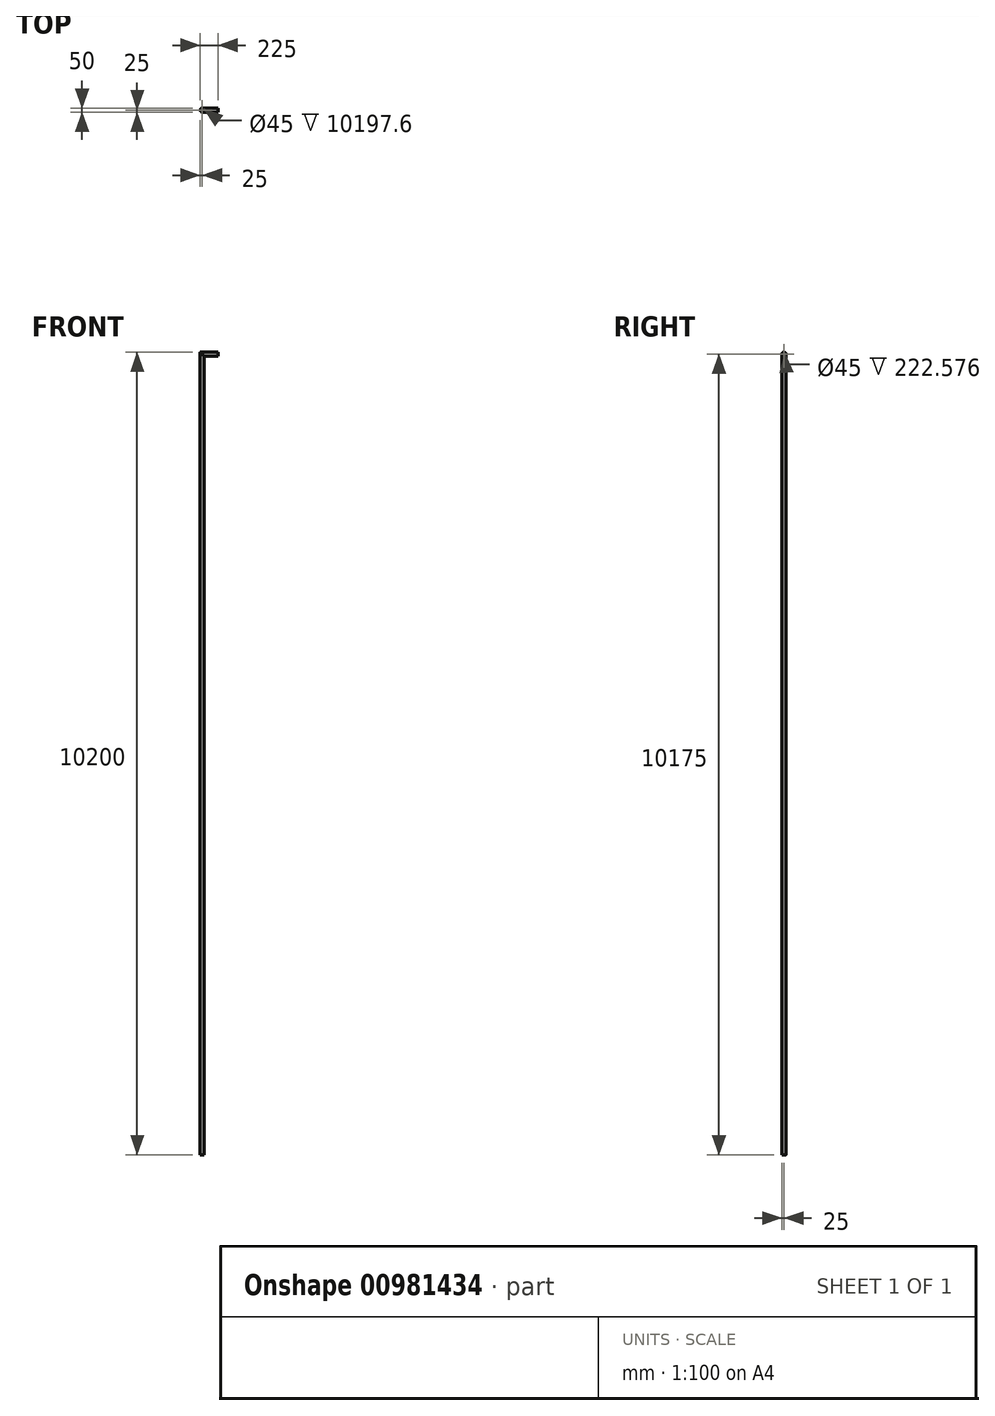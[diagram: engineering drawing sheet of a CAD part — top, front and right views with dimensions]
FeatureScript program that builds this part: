
annotation { "Feature Type Name" : "Feature", "Feature Type Description" : "" }
export const myFeature = defineFeature(function(context is Context, id is Id, definition is map)
    precondition{}
    {
        {
            var Q0;
            Q0=qCreatedBy(makeId("Front.planeOp"),FACE);
            var sketch = newSketch(context, id + "F0", { "sketchPlane" : qUnion([Q0])});
            skLineSegment(sketch, "E0.bottom", {"start": v(-25, 5100) * mm, "end": v(200, 5100) * mm});
            skLineSegment(sketch, "E0.top", {"start": v(-25, -5100) * mm, "end": v(25, -5100) * mm});
            skLineSegment(sketch, "E0.left", {"start": v(-25, 5100) * mm, "end": v(-25, -5100) * mm});
            skLineSegment(sketch, "E0.right", {"start": v(25, 5050) * mm, "end": v(25, -5100) * mm});
            skPoint(sketch, "E0.middle", {"position": v(0, 0) * mm});
            skLineSegment(sketch, "E1", {"start": v(200, 5100) * mm, "end": v(200, 5050) * mm});
            skLineSegment(sketch, "E2", {"start": v(200, 5050) * mm, "end": v(25, 5050) * mm});
            skSolve(sketch);
        }
        {
            var Q0;
            Q0 = qSketchRegion(id + "F0", true);
            extrude(context, id + "F1", {"entities" : qUnion([Q0]), "depth" : 50 * mm, "offsetDistance" : 25 * mm});
        }
        {
            var Q0;
            Q0=makeQuery(id+"F1.opExtrude","CAP_EDGE",EDGE,{"disambiguationData":[OSD([sQuery(id+"F0.wireOp",EDGE,"E0.bottom")])],"isStart":false});
            var Q1;
            Q1=makeQuery(id+"F1.opExtrude","CAP_EDGE",EDGE,{"disambiguationData":[OSD([sQuery(id+"F0.wireOp",EDGE,"E0.left")])],"isStart":false});
            var Q2;
            Q2=makeQuery(id+"F1.opExtrude","CAP_EDGE",EDGE,{"disambiguationData":[OSD([sQuery(id+"F0.wireOp",EDGE,"E2")])],"isStart":false});
            var Q3;
            Q3=makeQuery(id+"F1.opExtrude","CAP_EDGE",EDGE,{"disambiguationData":[OSD([sQuery(id+"F0.wireOp",EDGE,"E0.right")])],"isStart":false});
            var Q4;
            Q4=makeQuery(id+"F1.opExtrude","CAP_EDGE",EDGE,{"disambiguationData":[OSD([sQuery(id+"F0.wireOp",EDGE,"E2")])],"isStart":true});
            var Q5;
            Q5=makeQuery(id+"F1.opExtrude","CAP_EDGE",EDGE,{"disambiguationData":[OSD([sQuery(id+"F0.wireOp",EDGE,"E0.right")])],"isStart":true});
            var Q6;
            Q6=makeQuery(id+"F1.opExtrude","CAP_EDGE",EDGE,{"disambiguationData":[OSD([sQuery(id+"F0.wireOp",EDGE,"E0.bottom")])],"isStart":true});
            var Q7;
            Q7=makeQuery(id+"F1.opExtrude","CAP_EDGE",EDGE,{"disambiguationData":[OSD([sQuery(id+"F0.wireOp",EDGE,"E0.left")])],"isStart":true});
            fillet(context, id + "F2", {"entities" : qUnion([Q0, Q1, Q2, Q3, Q4, Q5, Q6, Q7]), "radius" : 25 * mm, "tangentPropagation" : true, "allowEdgeOverflow" : false});
        }
        {
            var Q0;
            Q0=makeQuery(id+"F1.opExtrude","SWEPT_FACE",FACE,{"disambiguationData":[OSD([sQuery(id+"F0.wireOp",EDGE,"E0.top")])]});
            var Q1;
            Q1=makeQuery(id+"F1.opExtrude","SWEPT_FACE",FACE,{"disambiguationData":[OSD([sQuery(id+"F0.wireOp",EDGE,"E1")])]});
            shell(context, id + "F3", {"entities" : qUnion([Q0, Q1]), "thickness" : 2.5 * mm});
        }
    });
